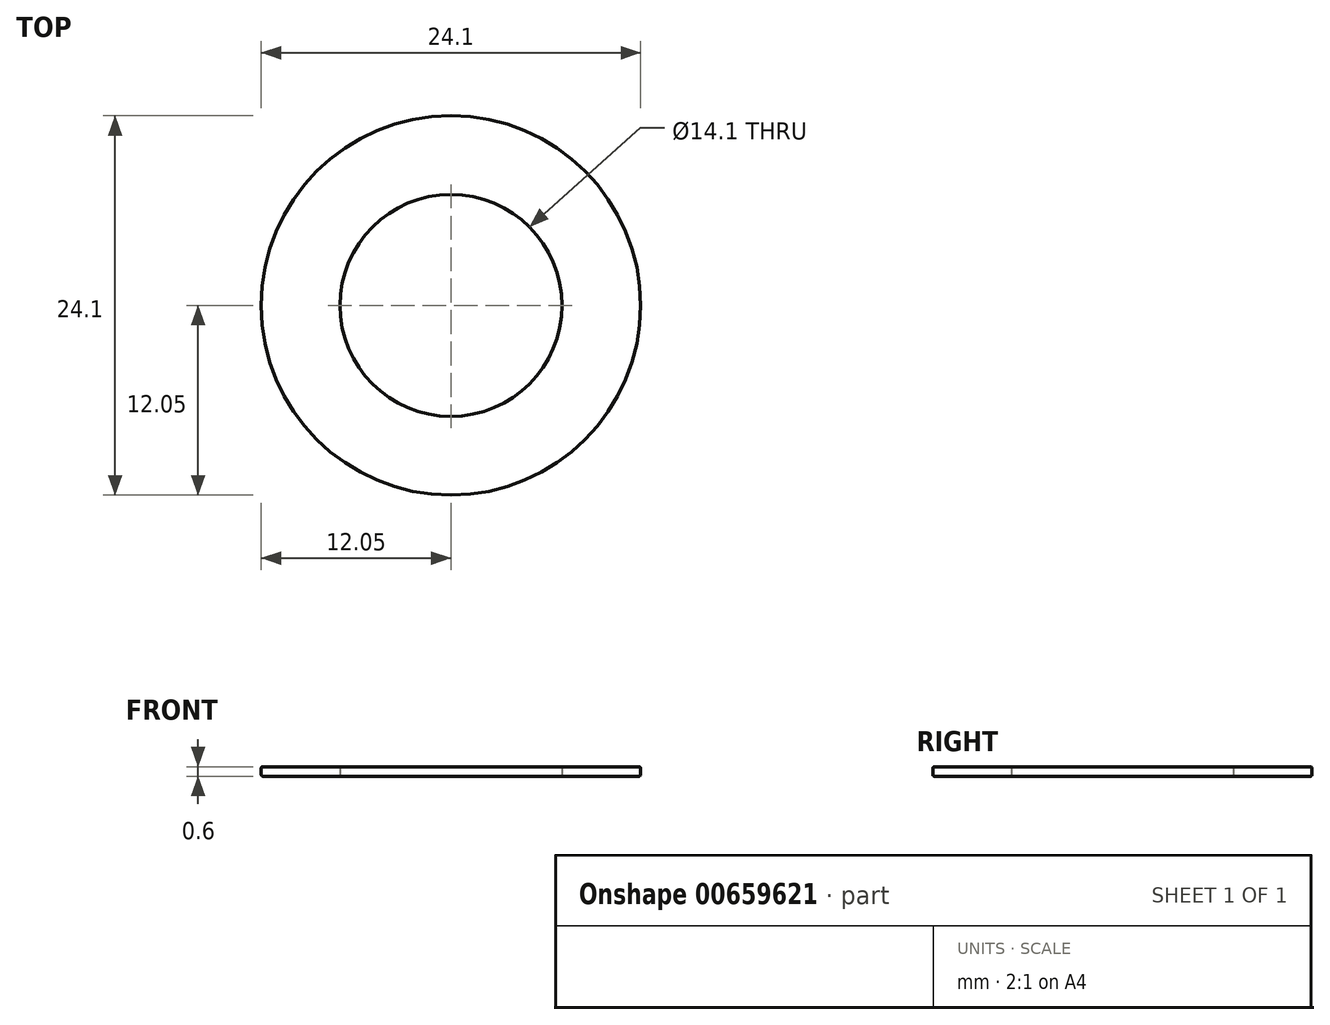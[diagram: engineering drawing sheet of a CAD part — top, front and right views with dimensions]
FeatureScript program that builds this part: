
annotation { "Feature Type Name" : "Feature", "Feature Type Description" : "" }
export const myFeature = defineFeature(function(context is Context, id is Id, definition is map)
    precondition{}
    {
        {
            var Q0;
            Q0=qCreatedBy(makeId("Top.planeOp"),FACE);
            var sketch = newSketch(context, id + "F0", { "sketchPlane" : qUnion([Q0])});
            skCircle(sketch, "E0", {"center": v(0, 0) * mm, "radius": 12.05 * mm});
            skCircle(sketch, "E1", {"center": v(0, 0) * mm, "radius": 7.05 * mm});
            skSolve(sketch);
        }
        {
            var Q0;
            Q0=makeQuery(id+"F0.imprint","IMPRINT",FACE,{"disambiguationData":[TD([[makeQuery(id+"F0.imprint","IMPRINT",EDGE,{"derivedFrom":sQuery(id+"F0.wireOp",EDGE,"E0")}),1.0]])]});
            extrude(context, id + "F1", {"entities" : qUnion([Q0]), "depth" : .6 * mm, "offsetDistance" : 25 * mm});
        }
        {
            var Q0;
            Q0=makeQuery(id+"F1.opExtrude","CAP_FACE",FACE,{"disambiguationData":[OSD([sQuery(id+"F0.wireOp",EDGE,"E0"),sQuery(id+"F0.wireOp",EDGE,"E1")])],"isStart":false});
            var Q1;
            Q1=makeQuery(id+"F1.opExtrude","CAP_FACE",FACE,{"disambiguationData":[OSD([sQuery(id+"F0.wireOp",EDGE,"E0"),sQuery(id+"F0.wireOp",EDGE,"E1")])],"isStart":true});
            fillet(context, id + "F2", {"entities" : qUnion([Q0, Q1]), "radius" : .1 * mm, "tangentPropagation" : true, "allowEdgeOverflow" : false});
        }
    });
